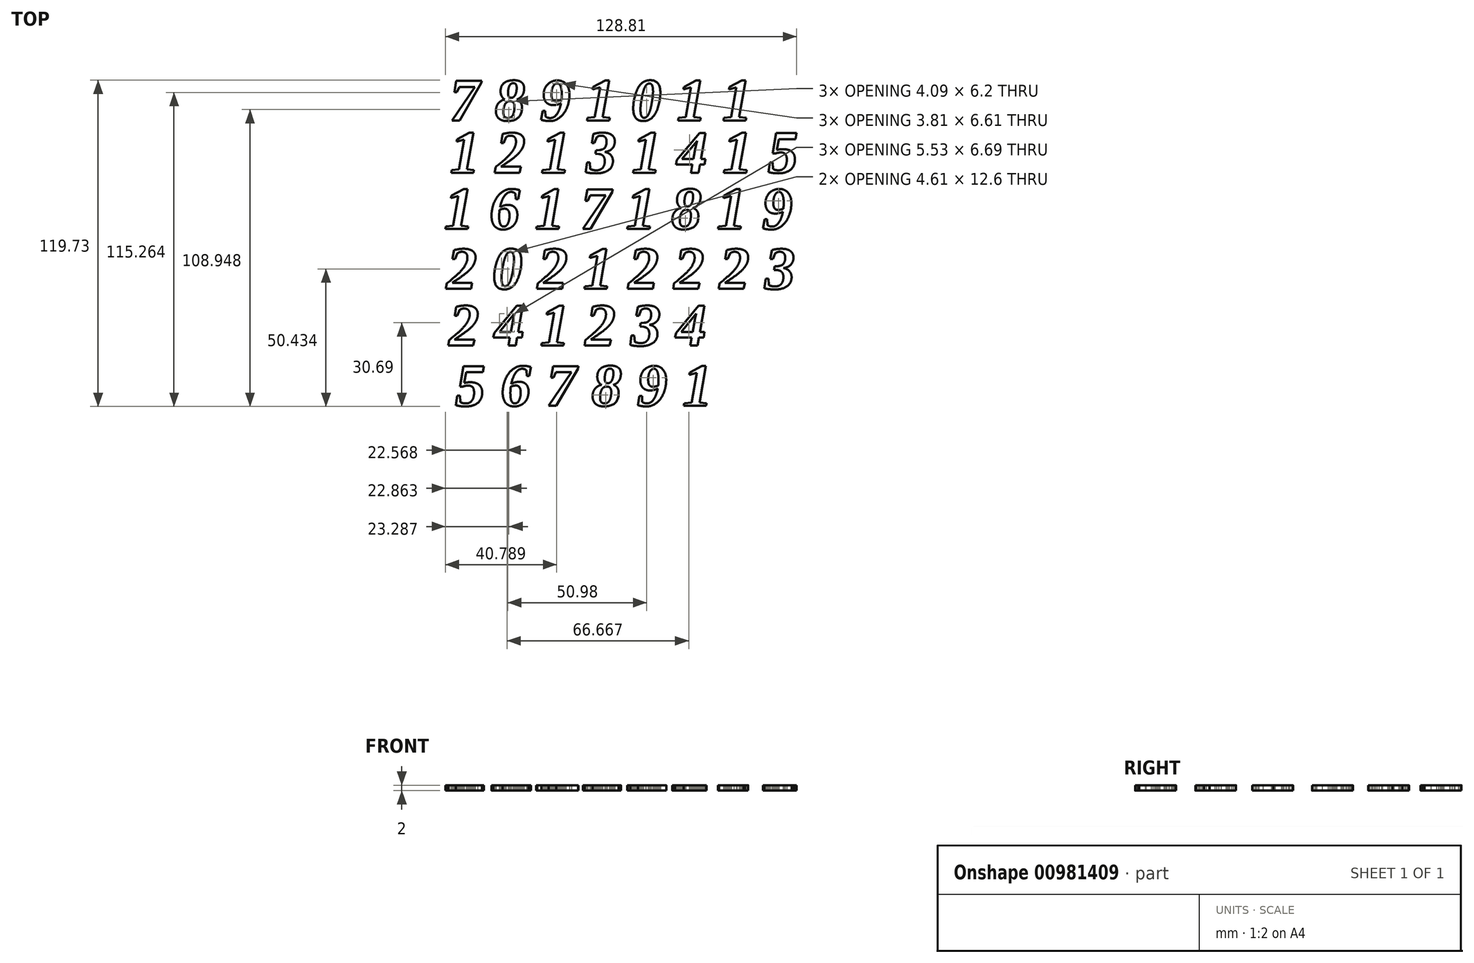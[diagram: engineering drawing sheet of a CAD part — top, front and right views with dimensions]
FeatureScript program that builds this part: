
annotation { "Feature Type Name" : "Feature", "Feature Type Description" : "" }
export const myFeature = defineFeature(function(context is Context, id is Id, definition is map)
    precondition{}
    {
        {
            var Q0;
            Q0=qCreatedBy(makeId("Top.planeOp"),FACE);
            var sketch = newSketch(context, id + "F0", { "sketchPlane" : qUnion([Q0])});
            skLineSegment(sketch, "E0.bottom", {"start": v(-70, -70) * mm, "end": v(70, -70) * mm, "construction": true});
            skLineSegment(sketch, "E0.top", {"start": v(-70, 70) * mm, "end": v(70, 70) * mm, "construction": true});
            skLineSegment(sketch, "E0.left", {"start": v(-70, -70) * mm, "end": v(-70, 70) * mm, "construction": true});
            skLineSegment(sketch, "E0.right", {"start": v(70, -70) * mm, "end": v(70, 70) * mm, "construction": true});
            skPoint(sketch, "E0.middle", {"position": v(0, 0) * mm});
            skText(sketch, "E1", { "text": "7 8 9 1 0 1 1", "fontName": "Tinos-BoldItalic.ttf"});
            skText(sketch, "E2", { "text": "1 2 1 3 1 4 1 5", "fontName": "Tinos-BoldItalic.ttf"});
            skText(sketch, "E3", { "text": "1 6 1 7 1 8 1 9", "fontName": "Tinos-BoldItalic.ttf"});
            skText(sketch, "E4", { "text": "2 0 2 1 2 2 2 3", "fontName": "Tinos-BoldItalic.ttf"});
            skText(sketch, "E5", { "text": "2 4 1 2 3 4", "fontName": "Tinos-BoldItalic.ttf"});
            skText(sketch, "E6", { "text": "5 6 7 8 9 1", "fontName": "Tinos-BoldItalic.ttf"});
            const initialGuessF0  = {"E1": [-0.06384, 0.04956, 1, 0, 0.016], "E2": [-0.06367, 0.03038, 1, 0, 0.016], "E3": [-0.0658, 0.00973, 1, 0, 0.016], "E4": [-0.06482, -0.01223, 1, 0, 0.016], "E5": [-0.064, -0.03304, 1, 0, 0.016], "E6": [-0.0617, -0.05517, 1, 0, 0.016]};
            skSetInitialGuess(sketch, initialGuessF0);
            skSolve(sketch);
        }
        {
            var Q0;
            Q0 = qSketchRegion(id + "F0", true);
            extrude(context, id + "F1", {"entities" : qUnion([Q0]), "depth" : 2 * mm, "offsetDistance" : 25 * mm});
        }
    });
